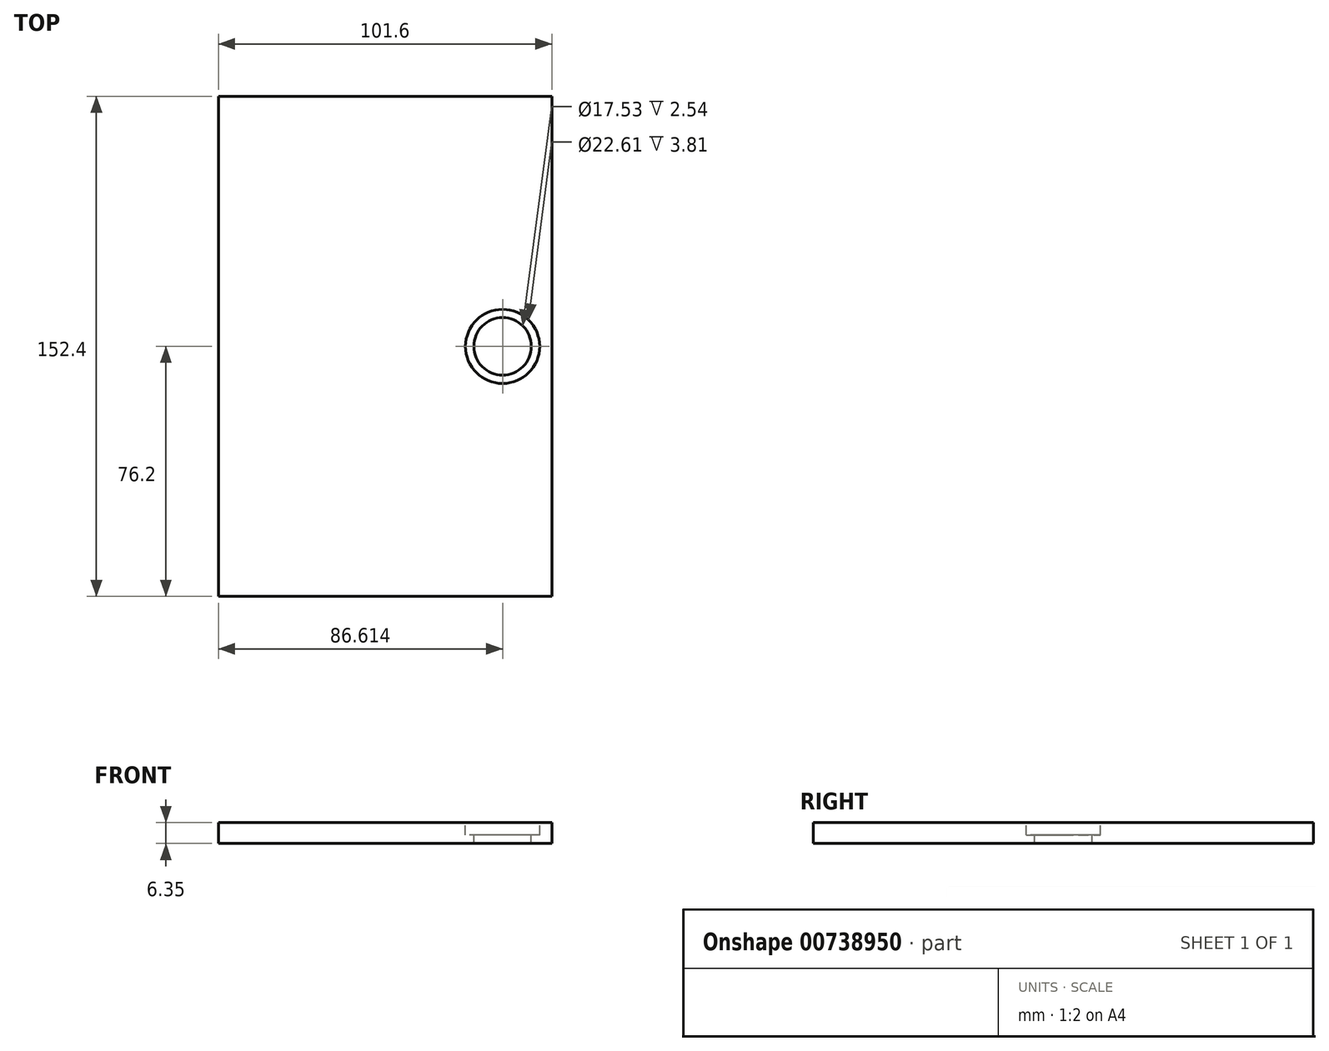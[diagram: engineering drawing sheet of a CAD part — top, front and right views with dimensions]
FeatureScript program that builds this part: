
annotation { "Feature Type Name" : "Feature", "Feature Type Description" : "" }
export const myFeature = defineFeature(function(context is Context, id is Id, definition is map)
    precondition{}
    {
        {
            var Q0;
            Q0=qCreatedBy(makeId("Top.planeOp"),FACE);
            var sketch = newSketch(context, id + "F0", { "sketchPlane" : qUnion([Q0])});
            skLineSegment(sketch, "E0.bottom", {"start": v(50.8, -76.2) * mm, "end": v(-50.8, -76.2) * mm});
            skLineSegment(sketch, "E0.top", {"start": v(50.8, 76.2) * mm, "end": v(-50.8, 76.2) * mm});
            skLineSegment(sketch, "E0.left", {"start": v(50.8, -76.2) * mm, "end": v(50.8, 76.2) * mm});
            skLineSegment(sketch, "E0.right", {"start": v(-50.8, -76.2) * mm, "end": v(-50.8, 76.2) * mm});
            skPoint(sketch, "E0.middle", {"position": v(0, 0) * mm});
            skSolve(sketch);
        }
        {
            var Q0;
            Q0=makeQuery(id+"F0.imprint","IMPRINT",FACE,{"disambiguationData":[TD([[makeQuery(id+"F0.imprint","IMPRINT",EDGE,{"derivedFrom":sQuery(id+"F0.wireOp",EDGE,"E0.bottom")}),-1.0]])]});
            extrude(context, id + "F1", {"entities" : qUnion([Q0]), "depth" : 6.35 * mm, "offsetDistance" : 25.4 * mm});
        }
        {
            var Q0;
            Q0=makeQuery(id+"F1.opExtrude","CAP_FACE",FACE,{"disambiguationData":[OSD([sQuery(id+"F0.wireOp",EDGE,"E0.bottom"),sQuery(id+"F0.wireOp",EDGE,"E0.top"),sQuery(id+"F0.wireOp",EDGE,"E0.left"),sQuery(id+"F0.wireOp",EDGE,"E0.right")])],"isStart":false});
            var sketch = newSketch(context, id + "F2", { "sketchPlane" : qUnion([Q0])});
            skPoint(sketch, "E1", {"position": v(35.81, 0) * mm});
            skLineSegment(sketch, "E2", {"start": v(35.81, -76.2) * mm, "end": v(35.81, 0) * mm});
            skLineSegment(sketch, "E3", {"start": v(50.8, 0) * mm, "end": v(35.81, 0) * mm});
            skSolve(sketch);
        }
        {
            var Q0;
            Q0=sQuery(id+"F2.wireOp",VERTEX,"E1");
            var Q1;
            Q1=makeQuery(id+"F1.opExtrude","SWEPT_BODY",BODY,{"disambiguationData":[OSD([sQuery(id+"F0.wireOp",EDGE,"E0.bottom"),sQuery(id+"F0.wireOp",EDGE,"E0.top"),sQuery(id+"F0.wireOp",EDGE,"E0.left"),sQuery(id+"F0.wireOp",EDGE,"E0.right")])]});
            hole(context, id + "F3", {"style" : HoleStyle.C_BORE, "endStyle" : HoleEndStyle.THROUGH, "holeDiameter" : 17.53 * mm, "cBoreDiameter" : 22.6 * mm, "cBoreDepth" : 3.8 * mm, "majorDiameter" : 6.35 * mm, "isTappedThrough" : true, "tappedDepth" : 12.7 * mm, "tapClearance" : 3, "locations" : qUnion([Q0]), "scope" : qUnion([Q1])});
        }
    });
